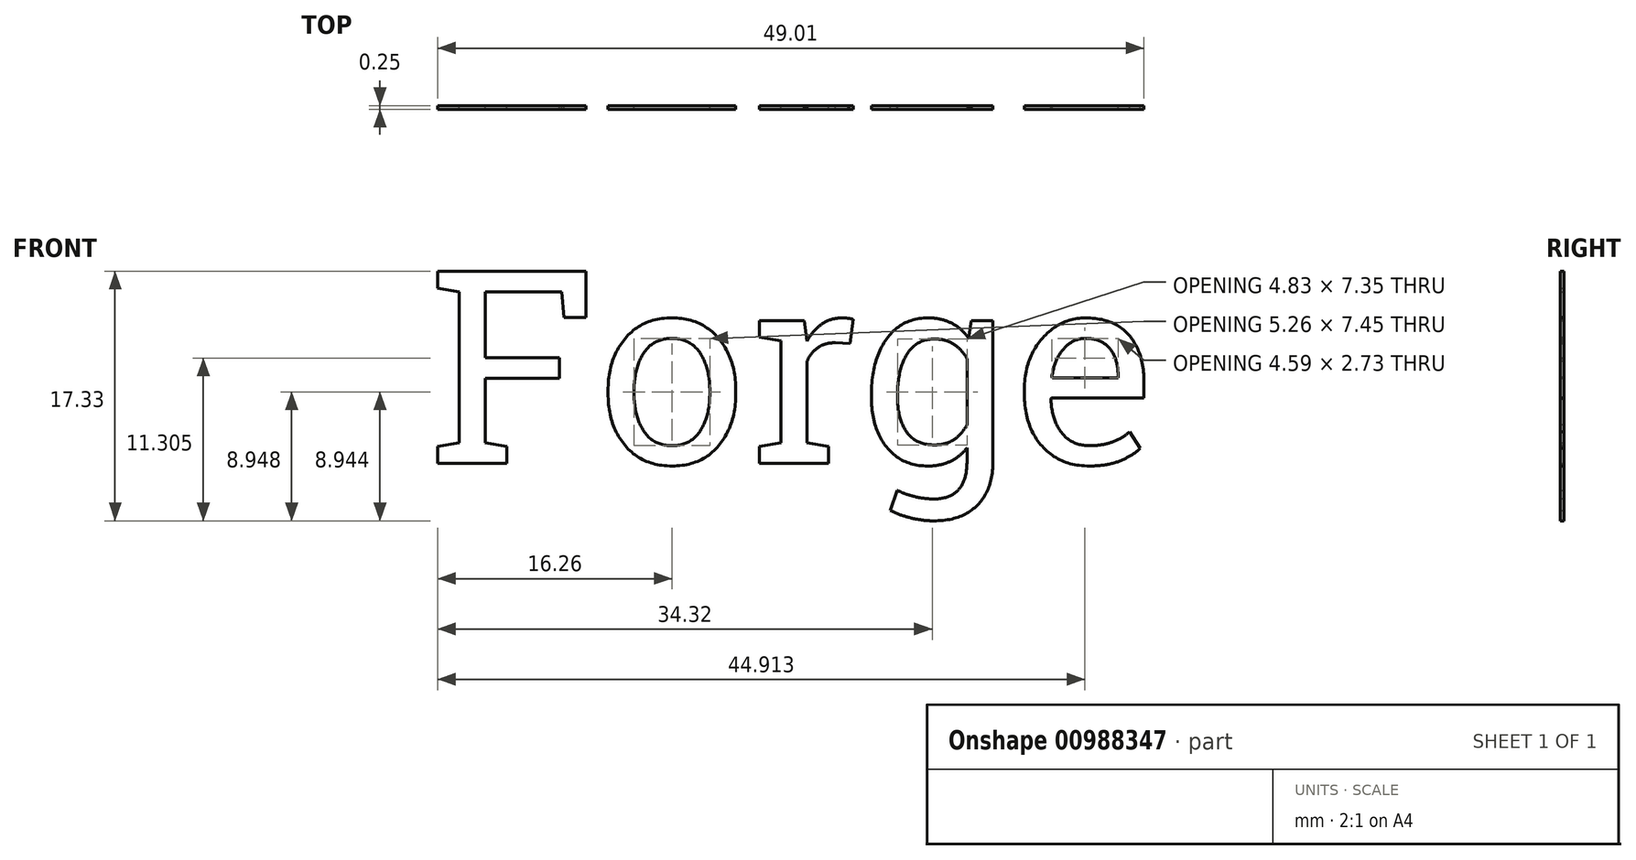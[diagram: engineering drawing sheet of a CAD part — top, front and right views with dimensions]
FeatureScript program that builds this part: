
annotation { "Feature Type Name" : "Feature", "Feature Type Description" : "" }
export const myFeature = defineFeature(function(context is Context, id is Id, definition is map)
    precondition{}
    {
        {
            var Q0;
            Q0=qCreatedBy(makeId("Front.planeOp"),FACE);
            var sketch = newSketch(context, id + "F0", { "sketchPlane" : qUnion([Q0])});
            skText(sketch, "E0", { "text": "Forge", "fontName": "RobotoSlab-Regular.ttf"});
            const initialGuessF0  = {"E0": [-0.0508, 0, 1, 0, 0.0135]};
            skSetInitialGuess(sketch, initialGuessF0);
            skSolve(sketch);
        }
        {
            var Q0;
            Q0=makeQuery(id+"F0.imprint","IMPRINT",FACE,{"disambiguationData":[TD([[makeQuery(id+"F0.imprint","IMPRINT",EDGE,{"derivedFrom":sQuery(id+"F0.wireOp",EDGE,"E0.sketch_text.stroke-0")}),-1.0]])]});
            var Q1;
            Q1=makeQuery(id+"F0.imprint","IMPRINT",FACE,{"disambiguationData":[TD([[makeQuery(id+"F0.imprint","IMPRINT",EDGE,{"derivedFrom":sQuery(id+"F0.wireOp",EDGE,"E0.sketch_text.stroke-18")}),-1.0]])]});
            var Q2;
            Q2=makeQuery(id+"F0.imprint","IMPRINT",FACE,{"disambiguationData":[TD([[makeQuery(id+"F0.imprint","IMPRINT",EDGE,{"derivedFrom":sQuery(id+"F0.wireOp",EDGE,"E0.sketch_text.stroke-38")}),-1.0]])]});
            var Q3;
            Q3=makeQuery(id+"F0.imprint","IMPRINT",FACE,{"disambiguationData":[TD([[makeQuery(id+"F0.imprint","IMPRINT",EDGE,{"derivedFrom":sQuery(id+"F0.wireOp",EDGE,"E0.sketch_text.stroke-57")}),-1.0]])]});
            var Q4;
            Q4=makeQuery(id+"F0.imprint","IMPRINT",FACE,{"disambiguationData":[TD([[makeQuery(id+"F0.imprint","IMPRINT",EDGE,{"derivedFrom":sQuery(id+"F0.wireOp",EDGE,"E0.sketch_text.stroke-89")}),-1.0]])]});
            extrude(context, id + "F1", {"entities" : qUnion([Q0, Q1, Q2, Q3, Q4]), "depth" : 0.25 * mm, "offsetDistance" : 25.4 * mm});
        }
    });
